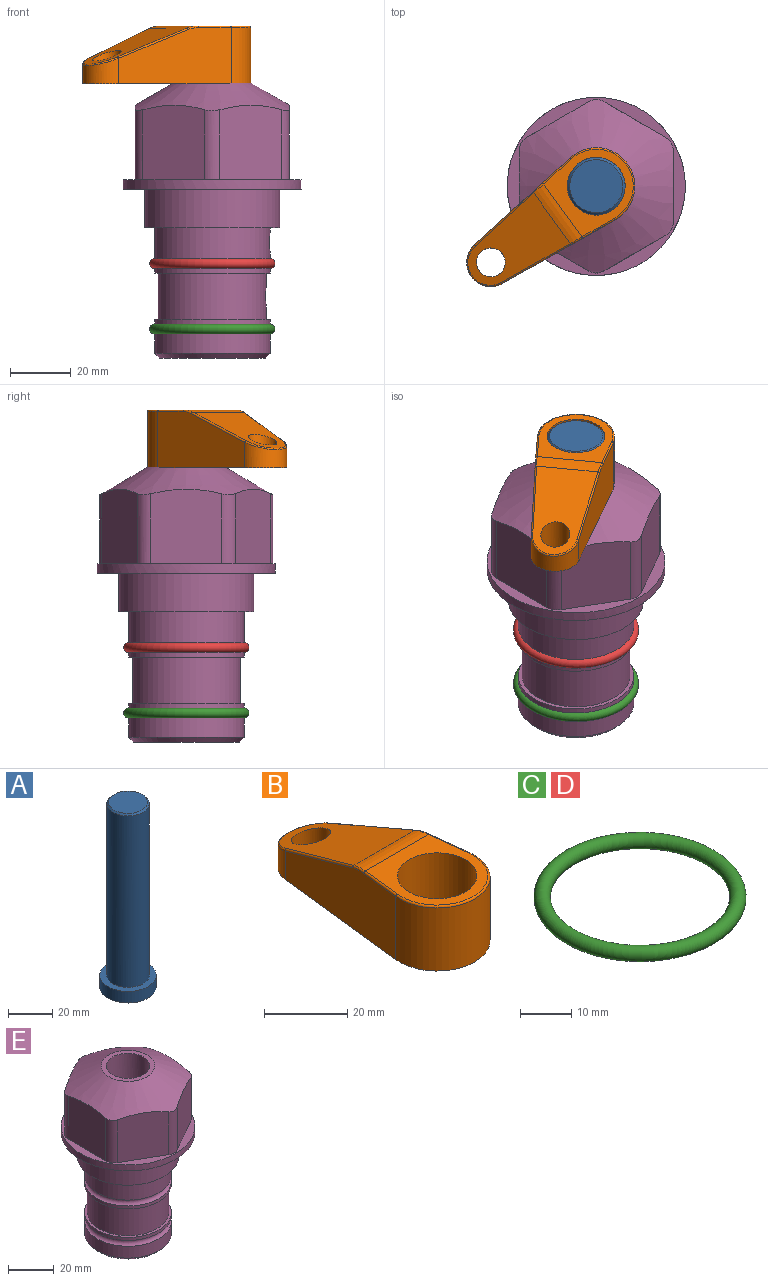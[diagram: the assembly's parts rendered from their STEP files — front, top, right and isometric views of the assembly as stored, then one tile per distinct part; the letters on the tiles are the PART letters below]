
ASSEMBLY  parts=5 mates=3
PART A: 6 faces, bbox 25.4x25.4x101.6 mm
  f0: plane 17.46x17.46mm, normal (0,0,1), area 239.5mm2, adj f5
  f1: plane 25.4x25.4mm, normal (0,0,-1), area 506.7mm2, adj f2
  f2: cylinder r=12.7mm len=25.4mm, axis (0,0,1), area 506.7mm2, adj f1,f3
  f3: plane 25.4x25.4mm, normal (0,0,1), area 221.7mm2, adj f2,f4
  f4: cylinder r=9.53mm len=94.46mm, axis (0,0,1), area 5653mm2, adj f3,f5
  f5: cone r=8.73mm half-angle=45deg, axis (0,0,-1), area 64.4mm2, adj f0,f4
PART B: 44 faces, bbox 27.5x64.5x19.1 mm
  f0: plane 2.3x0.95mm, normal (0,0,-1), area 1mm2, adj f25,f30,f34
  f1: plane 63.5x25.4mm, normal (0,0,-1), area 561.7mm2, adj f2,f3,f4,f5,f6,f7,f19,f20
  f2: cylinder r=12.7mm len=25.4mm, axis (0,0,-1), area 792.2mm2, adj f1,f3,f5,f13
  f3: plane 42.33x18.54mm, normal (0.99,0.11,0), area 647mm2, adj f1,f2,f4,f11,f12,f14
  f4: cylinder r=7.94mm len=15.78mm, axis (0,0,-1), area 158.6mm2, adj f1,f3,f5,f16
  f5: plane 42.33x18.54mm, normal (-0.99,0.11,0), area 647mm2, adj f1,f2,f4,f15,f17,f18
  f6: cylinder r=9.53mm len=19.05mm, axis (0,0,-1), area 1140.1mm2, adj f1,f8
  f7: cylinder r=4.76mm len=10.98mm, axis (0,0,-1), area 276.1mm2, adj f1,f9
  f8: plane 25.83x24.38mm, normal (0,0,1), area 262.2mm2, adj f6,f10,f11,f13,f15
  f9: plane 32.49x20.55mm, normal (0,0.34,0.94), area 489.9mm2, adj f7,f10,f14,f16,f18
  f10: cylinder r=12.7mm len=21.49mm, axis (-1,0,0), area 93.2mm2, adj f8,f9,f12,f17
  f11: cylinder r=0.51mm len=12.34mm, axis (0.11,-0.99,0), area 9.9mm2, adj f3,f8,f12,f13
  f12: bspline ~7.62x1.64mm, area 3.5mm2, adj f3,f10,f11,f14
  f13: torus R=12.19mm, axis (0,0,1), area 33.6mm2, adj f2,f8,f11,f15
  f14: cylinder r=0.51mm len=26.01mm, axis (0.1,-0.93,0.34), area 21.6mm2, adj f3,f9,f12,f16
  f15: cylinder r=0.51mm len=12.34mm, axis (0.11,0.99,0), area 9.9mm2, adj f5,f8,f13,f17
  f16: bspline ~15.78x7.05mm, area 15.7mm2, adj f4,f9,f14,f18
  f17: bspline ~7.62x1.64mm, area 3.5mm2, adj f5,f10,f15,f18
  f18: cylinder r=0.51mm len=26.01mm, axis (0.1,0.93,-0.34), area 21.6mm2, adj f5,f9,f16,f17
  f19: plane 21.6x14.29mm, normal (-0.99,-0.11,0), area 242.6mm2, adj f1,f26,f28,f34,f36,f38
  f20: plane 21.6x14.29mm, normal (0.99,-0.11,0), area 242.6mm2, adj f1,f27,f29,f37,f39,f41
  f21: cylinder r=12.7mm len=14.29mm, axis (0,0,-1), area 173.2mm2, adj f1,f26,f27,f30,f31,f33
  f22: cylinder r=7.94mm len=7.63mm, axis (0,0,-1), area 53.8mm2, adj f1,f28,f29,f42
  f23: plane 2.3x0.95mm, normal (0,0,-1), area 1mm2, adj f25,f33,f37
  f24: plane 17.94x12.32mm, normal (0,-0.34,-0.94), area 191.2mm2, adj f25,f38,f41,f42
  f25: cylinder r=9.53mm len=12.93mm, axis (-1,0,0), area 37.5mm2, adj f0,f23,f24,f31,f36,f39
  f26: cylinder r=1.59mm len=14.29mm, axis (0,0,-1), area 49mm2, adj f1,f19,f21,f32
  f27: cylinder r=1.59mm len=14.29mm, axis (0,0,-1), area 49mm2, adj f1,f20,f21,f35
  f28: cylinder r=1.59mm len=7.28mm, axis (0,0,-1), area 22.1mm2, adj f1,f19,f22,f40
  f29: cylinder r=1.59mm len=7.28mm, axis (0,0,-1), area 22.1mm2, adj f1,f20,f22,f43
  f30: torus R=14.29mm, axis (0,0,1), area 5.8mm2, adj f0,f21,f31,f32
  f31: bspline ~11.06x2.73mm, area 20.8mm2, adj f21,f25,f30,f33
  f32: sphere r=1.59mm, area 5.4mm2, adj f26,f30,f34
  f33: torus R=14.29mm, axis (0,0,1), area 5.8mm2, adj f21,f23,f31,f35
  f34: cylinder r=1.59mm len=1.68mm, axis (-0.11,0.99,0), area 2.4mm2, adj f0,f19,f32,f36
  f35: sphere r=1.59mm, area 5.4mm2, adj f27,f33,f37
  f36: bspline ~5.82x2.33mm, area 7.7mm2, adj f19,f25,f34,f38
  f37: cylinder r=1.59mm len=1.68mm, axis (0.11,0.99,0), area 2.4mm2, adj f20,f23,f35,f39
  f38: cylinder r=1.59mm len=18.33mm, axis (0.1,-0.93,0.34), area 46.7mm2, adj f19,f24,f36,f40
  f39: bspline ~5.82x2.33mm, area 7.7mm2, adj f20,f25,f37,f41
  f40: sphere r=1.59mm, area 3.6mm2, adj f28,f38,f42
  f41: cylinder r=1.59mm len=18.33mm, axis (0.1,0.93,-0.34), area 46.7mm2, adj f20,f24,f39,f43
  f42: bspline ~8.31x1.84mm, area 15.3mm2, adj f22,f24,f40,f43
  f43: sphere r=1.59mm, area 3.6mm2, adj f29,f41,f42
PART C: 1 faces, bbox 44.7x44.7x3.2 mm
  f0: torus R=19.05mm, axis (0,0,1), area 1193.9mm2
PART D: same geometry as C
PART E: 36 faces, bbox 58.7x58.7x91.2 mm
  f0: cylinder r=17.78mm len=35.56mm, axis (0,0,1), area 1670.8mm2, adj f23,f24,f31
  f1: cylinder r=19.05mm len=38.1mm, axis (0,0,1), area 1191.9mm2, adj f26,f27,f30
  f2: plane 58.66x58.66mm, normal (0,0,-1), area 1150.6mm2, adj f3,f28
  f3: cylinder r=29.33mm len=58.66mm, axis (0,0,-1), area 585.1mm2, adj f2,f4
  f4: plane 58.66x58.66mm, normal (0,0,1), area 475.9mm2, adj f3,f5,f6,f7,f8,f9,f10,f11
  f5: plane 24.5x20.32mm, normal (0.5,-0.87,0), area 562.8mm2, adj f4,f15,f16,f17
  f6: plane 24.5x20.32mm, normal (-0.5,-0.87,0), area 562.8mm2, adj f4,f14,f15,f17
  f7: plane 24.5x23.48mm, normal (-1,0,0), area 562.8mm2, adj f4,f13,f14,f17
  f8: plane 24.5x20.32mm, normal (-0.5,0.87,0), area 562.8mm2, adj f4,f12,f13,f17
  f9: plane 24.5x20.32mm, normal (0.5,0.87,0), area 562.8mm2, adj f4,f11,f12,f17
  f10: plane 24.5x23.48mm, normal (1,0,0), area 562.8mm2, adj f4,f11,f16,f17
  f11: cylinder r=5.08mm len=23.01mm, axis (0,0,-1), area 121.2mm2, adj f4,f9,f10,f17
  f12: cylinder r=5.08mm len=23.01mm, axis (0,0,-1), area 121.2mm2, adj f4,f8,f9,f17
  f13: cylinder r=5.08mm len=23.01mm, axis (0,0,-1), area 121.2mm2, adj f4,f7,f8,f17
  f14: cylinder r=5.08mm len=23.01mm, axis (0,0,-1), area 121.2mm2, adj f4,f6,f7,f17
  f15: cylinder r=5.08mm len=23.01mm, axis (0,0,-1), area 121.2mm2, adj f4,f5,f6,f17
  f16: cylinder r=5.08mm len=23.01mm, axis (0,0,-1), area 121.2mm2, adj f4,f5,f10,f17
  f17: cone r=11.73mm half-angle=60deg, axis (0,0,-1), area 2071.8mm2, adj f5,f6,f7,f8,f9,f10,f11,f12
  f18: plane 23.46x23.46mm, normal (0,0,1), area 147.4mm2, adj f17,f35
  f19: plane 34.93x34.93mm, normal (0,0,-1), area 958mm2, adj f29
  f20: cylinder r=19.05mm len=38.1mm, axis (0,0,1), area 760.1mm2, adj f21,f29
  f21: torus R=19.05mm, axis (0,0,1), area 565.3mm2, adj f20,f22
  f22: cylinder r=19.05mm len=38.1mm, axis (0,0,1), area 190mm2, adj f21,f23
  f23: plane 38.1x38.1mm, normal (0,0,1), area 146.9mm2, adj f0,f22
  f24: plane 38.1x38.1mm, normal (0,0,-1), area 146.9mm2, adj f0,f25
  f25: cylinder r=19.05mm len=38.1mm, axis (0,0,1), area 190mm2, adj f24,f26
  f26: torus R=19.05mm, axis (0,0,1), area 565.3mm2, adj f1,f25
  f27: plane 44.45x44.45mm, normal (0,0,-1), area 411.7mm2, adj f1,f28
  f28: cylinder r=22.23mm len=44.45mm, axis (0,0,1), area 1773.5mm2, adj f2,f27
  f29: cone r=19.05mm half-angle=45deg, axis (0,0,1), area 257.5mm2, adj f19,f20
  f30: cylinder r=3.17mm len=6.75mm, axis (-1,0,0), area 128mm2, adj f1,f33
  f31: cylinder r=3.17mm len=6.35mm, axis (-1,0,0), area 102.5mm2, adj f0,f33
  f32: plane 25.4x25.4mm, normal (0,0,1), area 506.7mm2, adj f33
  f33: cylinder r=12.7mm len=66.42mm, axis (0,0,-1), area 5236.2mm2, adj f30,f31,f32,f34
  f34: cone r=9.53mm half-angle=30deg, axis (0,0,-1), area 443.4mm2, adj f33,f35
  f35: cylinder r=9.53mm len=19.05mm, axis (0,0,-1), area 849mm2, adj f18,f34
PLACE A rot(axis=(0,0,-1),144.1deg) t=(0,0,-19.9)mm
PLACE B rot(axis=(0,0,1),125.9deg) t=(0,0,34.71)mm
PLACE C t=(0,0,-21.59)mm
PLACE D at identity
PLACE E at identity fixed
MATE fastened C.f0 <-> E.f0  axis (0,0,1) through (0,0,-46.1)mm
MATE cylindrical A.f2 <-> E.f0  axis (0,0,1) through (0,0,5.74)mm
MATE fastened B.f2 <-> A.f2  axis (0,0,1) through (0,0,53.76)mm
